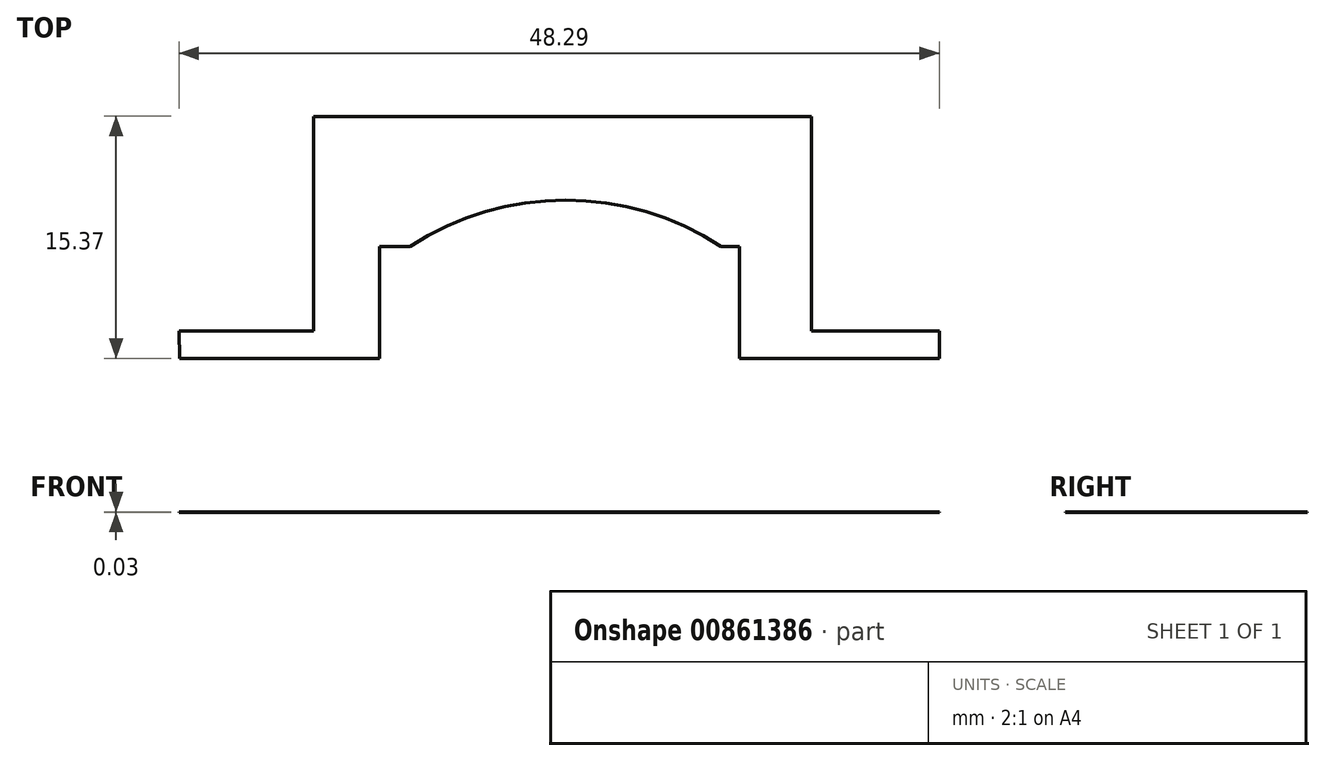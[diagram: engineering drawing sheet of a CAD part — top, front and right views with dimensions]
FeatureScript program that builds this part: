
annotation { "Feature Type Name" : "Feature", "Feature Type Description" : "" }
export const myFeature = defineFeature(function(context is Context, id is Id, definition is map)
    precondition{}
    {
        {
            var Q0;
            Q0=qCreatedBy(makeId("Top.planeOp"),FACE);
            var sketch = newSketch(context, id + "F0", { "sketchPlane" : qUnion([Q0])});
            skLineSegment(sketch, "E0", {"start": v(-1.75, 0) * mm, "end": v(-14.45, 0) * mm});
            skLineSegment(sketch, "E1", {"start": v(-14.45, 7.11) * mm, "end": v(-37.31, 7.11) * mm});
            skLineSegment(sketch, "E2", {"start": v(-37.31, 7.11) * mm, "end": v(-37.31, 0) * mm});
            skLineSegment(sketch, "E3", {"start": v(-37.31, 0) * mm, "end": v(-50.01, 0) * mm});
            skLineSegment(sketch, "E4", {"start": v(-1.75, 0) * mm, "end": v(-1.75, 1.74) * mm});
            skLineSegment(sketch, "E5", {"start": v(-1.75, 1.74) * mm, "end": v(-9.86, 1.74) * mm});
            skLineSegment(sketch, "E6", {"start": v(-9.86, 1.74) * mm, "end": v(-9.86, 15.37) * mm});
            skLineSegment(sketch, "E7", {"start": v(-9.86, 15.37) * mm, "end": v(-41.48, 15.37) * mm});
            skLineSegment(sketch, "E8", {"start": v(-41.48, 15.37) * mm, "end": v(-41.48, 1.74) * mm});
            skLineSegment(sketch, "E9", {"start": v(-41.48, 1.74) * mm, "end": v(-50.04, 1.74) * mm});
            skLineSegment(sketch, "E10", {"start": v(-50.04, 1.74) * mm, "end": v(-50.01, 0) * mm});
            skLineSegment(sketch, "E11", {"start": v(-14.45, 7.11) * mm, "end": v(-14.45, 0) * mm});
            skSolve(sketch);
        }
        {
            var Q0;
            Q0=makeQuery(id+"F0.imprint","IMPRINT",FACE,{"disambiguationData":[TD([[makeQuery(id+"F0.imprint","IMPRINT",EDGE,{"derivedFrom":sQuery(id+"F0.wireOp",EDGE,"FpMA9RLA-SlnW-WJwS-gmap-vUzqFKgUysER")}),-1.0]])]});
            var Q1;
            Q1=makeQuery(id+"F0.imprint","IMPRINT",FACE,{"disambiguationData":[TD([[makeQuery(id+"F0.imprint","IMPRINT",EDGE,{"derivedFrom":sQuery(id+"F0.wireOp",EDGE,"E0")}),-1.0]])]});
            extrude(context, id + "F1", {"entities" : qUnion([Q0, Q1]), "depth" : 11 / 406.4 * mm, "offsetDistance" : 25.4 * mm});
        }
        {
            var Q0;
            Q0=makeQuery(id+"F1.opExtrude","SWEPT_FACE",FACE,{"disambiguationData":[OSD([sQuery(id+"F0.wireOp",EDGE,"E5")])]});
            var sketch = newSketch(context, id + "F2", { "sketchPlane" : qUnion([Q0])});
            skCircle(sketch, "E12", {"center": v(5.75, 8.83) * mm, "radius": 2.1 * mm});
            skSolve(sketch);
        }
        {
            var Q0;
            Q0=makeQuery(id+"F2.imprint","IMPRINT",FACE,{"disambiguationData":[TD([[makeQuery(id+"F2.imprint","IMPRINT",EDGE,{"derivedFrom":sQuery(id+"F2.wireOp",EDGE,"E12")}),1.0]])]});
            var Q1;
            Q1=sQuery(id+"F2.wireOp",EDGE,"E12");
            extrude(context, id + "F3", {"entities" : qUnion([Q0]), "operationType" : NewBodyOperationType.REMOVE, "surfaceEntities" : qUnion([Q1]), "oppositeDirection" : true, "depth" : 25.4 * mm, "offsetDistance" : 25.4 * mm});
        }
        {
            var Q0;
            Q0=makeQuery(id+"F1.opExtrude","SWEPT_FACE",FACE,{"disambiguationData":[OSD([sQuery(id+"F0.wireOp",EDGE,"E9")])]});
            var sketch = newSketch(context, id + "F4", { "sketchPlane" : qUnion([Q0])});
            skCircle(sketch, "E13", {"center": v(46.05, 7.92) * mm, "radius": 2.05 * mm});
            skSolve(sketch);
        }
        {
            var Q0;
            Q0=makeQuery(id+"F4.imprint","IMPRINT",FACE,{"disambiguationData":[TD([[makeQuery(id+"F4.imprint","IMPRINT",EDGE,{"derivedFrom":sQuery(id+"F4.wireOp",EDGE,"E13")}),1.0]])]});
            extrude(context, id + "F5", {"entities" : qUnion([Q0]), "operationType" : NewBodyOperationType.REMOVE, "oppositeDirection" : true, "depth" : 25.4 * mm, "offsetDistance" : 25.4 * mm});
        }
        {
            var Q0;
            Q0=makeQuery(id+"F1.opExtrude","CAP_FACE",FACE,{"disambiguationData":[OSD([sQuery(id+"F0.wireOp",EDGE,"E0"),sQuery(id+"F0.wireOp",EDGE,"E1"),sQuery(id+"F0.wireOp",EDGE,"E2"),sQuery(id+"F0.wireOp",EDGE,"E3"),sQuery(id+"F0.wireOp",EDGE,"E4"),sQuery(id+"F0.wireOp",EDGE,"E5"),sQuery(id+"F0.wireOp",EDGE,"E6"),sQuery(id+"F0.wireOp",EDGE,"E7"),sQuery(id+"F0.wireOp",EDGE,"E8"),sQuery(id+"F0.wireOp",EDGE,"E9"),sQuery(id+"F0.wireOp",EDGE,"E10"),sQuery(id+"F0.wireOp",EDGE,"E11")])],"isStart":true});
            var sketch = newSketch(context, id + "F6", { "sketchPlane" : qUnion([Q0])});
            skArc(sketch, "E14", {"start": v(-35.35, -7.11) * mm, "mid": v(-25.48, -10.04) * mm, "end": v(-15.6, -7.11) * mm});
            skLineSegment(sketch, "E15", {"start": v(-15.6, -7.11) * mm, "end": v(-35.35, -7.11) * mm});
            skSolve(sketch);
        }
        {
            var Q0;
            Q0=makeQuery(id+"F6.imprint","IMPRINT",FACE,{"disambiguationData":[TD([[makeQuery(id+"F6.imprint","IMPRINT",EDGE,{"derivedFrom":sQuery(id+"F6.wireOp",EDGE,"E14")}),1.0]])]});
            extrude(context, id + "F7", {"entities" : qUnion([Q0]), "operationType" : NewBodyOperationType.REMOVE, "oppositeDirection" : true, "depth" : 25.4 * mm, "offsetDistance" : 25.4 * mm});
        }
    });
